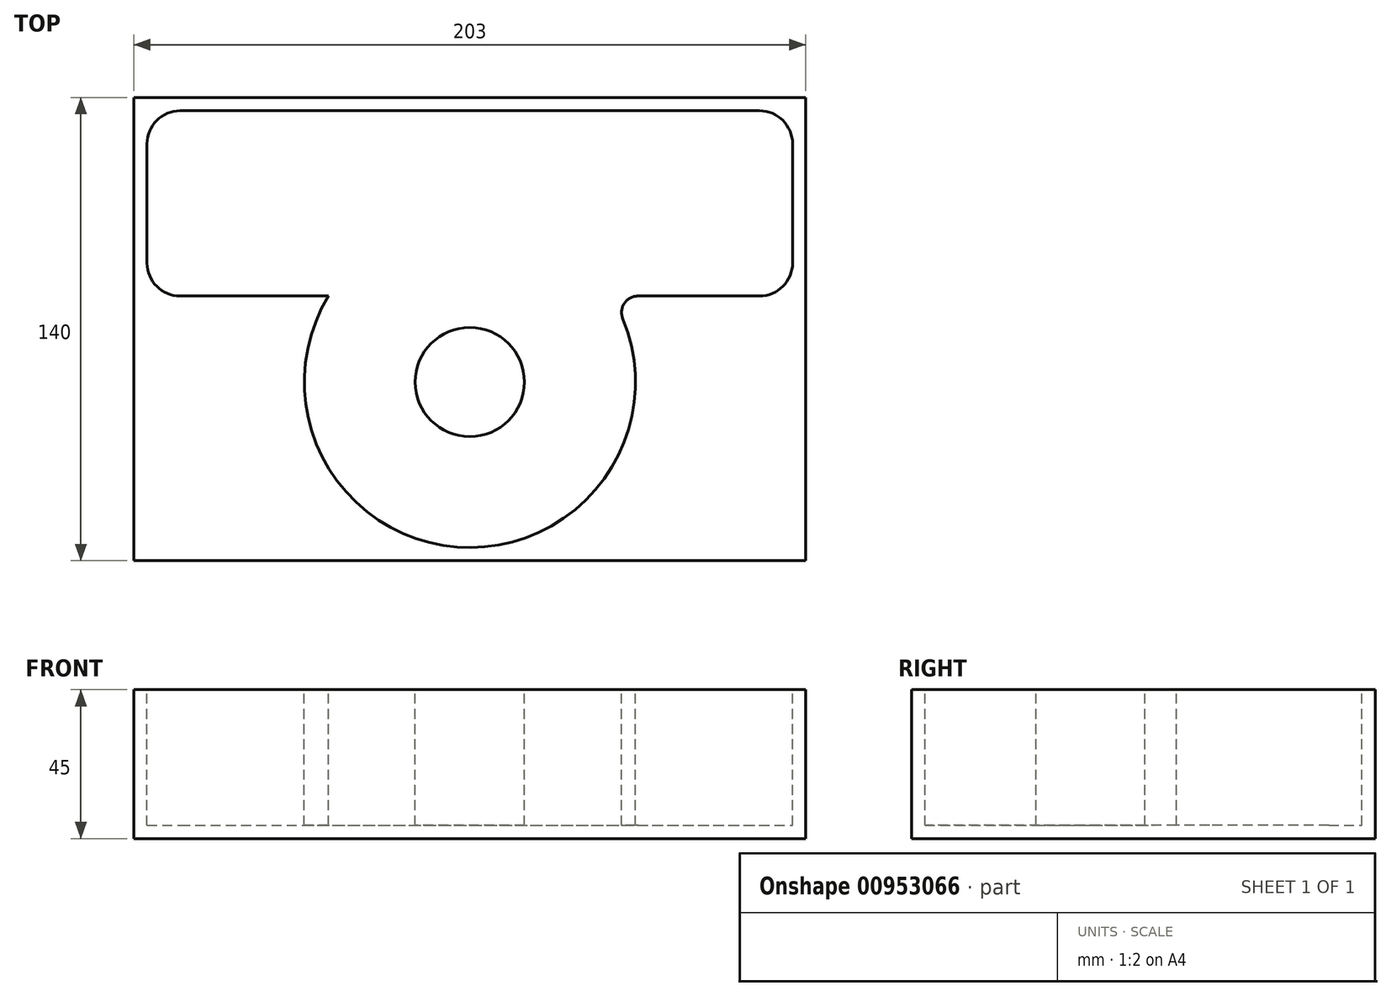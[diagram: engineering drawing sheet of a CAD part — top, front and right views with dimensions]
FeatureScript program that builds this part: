
annotation { "Feature Type Name" : "Feature", "Feature Type Description" : "" }
export const myFeature = defineFeature(function(context is Context, id is Id, definition is map)
    precondition{}
    {
        {
            var Q0;
            Q0=qCreatedBy(makeId("Top.planeOp"),FACE);
            var sketch = newSketch(context, id + "F0", { "sketchPlane" : qUnion([Q0])});
            skLineSegment(sketch, "E0.bottom", {"start": v(101.5, -70) * mm, "end": v(-101.5, -70) * mm});
            skLineSegment(sketch, "E0.top", {"start": v(101.5, 70) * mm, "end": v(-101.5, 70) * mm});
            skLineSegment(sketch, "E0.left", {"start": v(101.5, -70) * mm, "end": v(101.5, 70) * mm});
            skLineSegment(sketch, "E0.right", {"start": v(-101.5, -70) * mm, "end": v(-101.5, 70) * mm});
            skPoint(sketch, "E0.middle", {"position": v(0, 0) * mm});
            skSolve(sketch);
        }
        {
            var Q0;
            Q0=makeQuery(id+"F0.imprint","IMPRINT",FACE,{"disambiguationData":[TD([[makeQuery(id+"F0.imprint","IMPRINT",EDGE,{"derivedFrom":sQuery(id+"F0.wireOp",EDGE,"E0.bottom")}),-1.0]])]});
            extrude(context, id + "F1", {"entities" : qUnion([Q0]), "depth" : 45 * mm, "offsetDistance" : 25 * mm});
        }
        {
            var Q0;
            Q0=makeQuery(id+"F1.opExtrude","CAP_FACE",FACE,{"disambiguationData":[OSD([sQuery(id+"F0.wireOp",EDGE,"E0.bottom"),sQuery(id+"F0.wireOp",EDGE,"E0.top"),sQuery(id+"F0.wireOp",EDGE,"E0.left"),sQuery(id+"F0.wireOp",EDGE,"E0.right")])],"isStart":false});
            var sketch = newSketch(context, id + "F2", { "sketchPlane" : qUnion([Q0])});
            skLineSegment(sketch, "E1.bottom", {"start": v(-97.5, 66) * mm, "end": v(97.5, 66) * mm});
            skLineSegment(sketch, "E1.top", {"start": v(-97.5, 10) * mm, "end": v(97.5, 10) * mm});
            skLineSegment(sketch, "E1.left", {"start": v(-97.5, 66) * mm, "end": v(-97.5, 10) * mm});
            skLineSegment(sketch, "E1.right", {"start": v(97.5, 66) * mm, "end": v(97.5, 10) * mm});
            skSolve(sketch);
        }
        {
            var Q0;
            Q0=makeQuery(id+"F2.imprint","IMPRINT",FACE,{"disambiguationData":[TD([[makeQuery(id+"F2.imprint","IMPRINT",EDGE,{"derivedFrom":sQuery(id+"F2.wireOp",EDGE,"E1.bottom")}),-1.0]])]});
            extrude(context, id + "F3", {"entities" : qUnion([Q0]), "operationType" : NewBodyOperationType.REMOVE, "oppositeDirection" : true, "depth" : 41 * mm, "offsetDistance" : 25 * mm});
        }
        {
            var Q0;
            Q0=makeQuery(id+"F1.opExtrude","CAP_FACE",FACE,{"disambiguationData":[OSD([sQuery(id+"F0.wireOp",EDGE,"E0.bottom"),sQuery(id+"F0.wireOp",EDGE,"E0.top"),sQuery(id+"F0.wireOp",EDGE,"E0.left"),sQuery(id+"F0.wireOp",EDGE,"E0.right")])],"isStart":false});
            var sketch = newSketch(context, id + "F4", { "sketchPlane" : qUnion([Q0])});
            skCircle(sketch, "E2", {"center": v(0, -16) * mm, "radius": 50 * mm});
            skCircle(sketch, "E3", {"center": v(0, -16) * mm, "radius": 16.5 * mm});
            skSolve(sketch);
        }
        {
            var Q0;
            Q0=makeQuery(id+"F4.imprint","IMPRINT",FACE,{"disambiguationData":[TD([[makeQuery(id+"F4.imprint","IMPRINT",EDGE,{"derivedFrom":sQuery(id+"F4.wireOp",EDGE,"E3")}),-1.0]])]});
            extrude(context, id + "F5", {"entities" : qUnion([Q0]), "operationType" : NewBodyOperationType.REMOVE, "oppositeDirection" : true, "depth" : 41 * mm, "offsetDistance" : 25 * mm});
        }
        {
            var Q0;
            Q0=makeQuery(id+"F3.boolean.opBoolean","COPY",EDGE,{"derivedFrom":makeQuery(id+"F3.opExtrude","SWEPT_EDGE",EDGE,{"disambiguationData":[OSD([sQuery(id+"F2.wireOp",EDGE,"E1.bottom"),sQuery(id+"F2.wireOp",EDGE,"E1.right")])]})});
            var Q1;
            Q1=makeQuery(id+"F3.boolean.opBoolean","COPY",EDGE,{"derivedFrom":makeQuery(id+"F3.opExtrude","SWEPT_EDGE",EDGE,{"disambiguationData":[OSD([sQuery(id+"F2.wireOp",EDGE,"E1.bottom"),sQuery(id+"F2.wireOp",EDGE,"E1.left")])]})});
            var Q2;
            Q2=makeQuery(id+"F3.boolean.opBoolean","COPY",EDGE,{"derivedFrom":makeQuery(id+"F3.opExtrude","SWEPT_EDGE",EDGE,{"disambiguationData":[OSD([sQuery(id+"F2.wireOp",EDGE,"E1.top"),sQuery(id+"F2.wireOp",EDGE,"E1.right")])]})});
            var Q3;
            Q3=makeQuery(id+"F3.boolean.opBoolean","COPY",EDGE,{"derivedFrom":makeQuery(id+"F3.opExtrude","SWEPT_EDGE",EDGE,{"disambiguationData":[OSD([sQuery(id+"F2.wireOp",EDGE,"E1.top"),sQuery(id+"F2.wireOp",EDGE,"E1.left")])]})});
            fillet(context, id + "F6", {"entities" : qUnion([Q0, Q1, Q2, Q3]), "radius" : 10 * mm, "tangentPropagation" : true, "allowEdgeOverflow" : false});
        }
        {
            var Q0;
            {var subQ0=sQuery(id+"F4.wireOp",EDGE,"E2");var subQ1=sQuery(id+"F2.wireOp",EDGE,"E1.top");Q0=makeQuery(id+"F5.boolean.opBoolean","COPY",EDGE,{"derivedFrom":makeQuery(id+"F5.opExtrude","SWEPT_EDGE",EDGE,{"disambiguationData":[OSD([subQ1,subQ0]),TDD([makeQuery(id+"F4.imprint","INTERSECT",VERTEX,{"disambiguationData":[OD(1.0)],"derivedFrom":[makeQuery(id+"F3.boolean.opBoolean","COPY",EDGE,{"derivedFrom":makeQuery(id+"F3.opExtrude","CAP_EDGE",EDGE,{"disambiguationData":[OSD([subQ1])],"isStart":true})}),subQ0]})])]})});}
            var Q1;
            {var subQ0=sQuery(id+"F4.wireOp",EDGE,"E2");var subQ1=sQuery(id+"F2.wireOp",EDGE,"E1.top");Q1=makeQuery(id+"F5.boolean.opBoolean","COPY",EDGE,{"derivedFrom":makeQuery(id+"F5.opExtrude","SWEPT_EDGE",EDGE,{"disambiguationData":[OSD([subQ1,subQ0]),TDD([makeQuery(id+"F4.imprint","INTERSECT",VERTEX,{"disambiguationData":[OD(0.0)],"derivedFrom":[makeQuery(id+"F3.boolean.opBoolean","COPY",EDGE,{"derivedFrom":makeQuery(id+"F3.opExtrude","CAP_EDGE",EDGE,{"disambiguationData":[OSD([subQ1])],"isStart":true})}),subQ0]})])]})});}
            fillet(context, id + "F7", {"entities" : qUnion([Q0, Q1]), "radius" : 5 * mm, "tangentPropagation" : true, "allowEdgeOverflow" : false});
        }
    });
